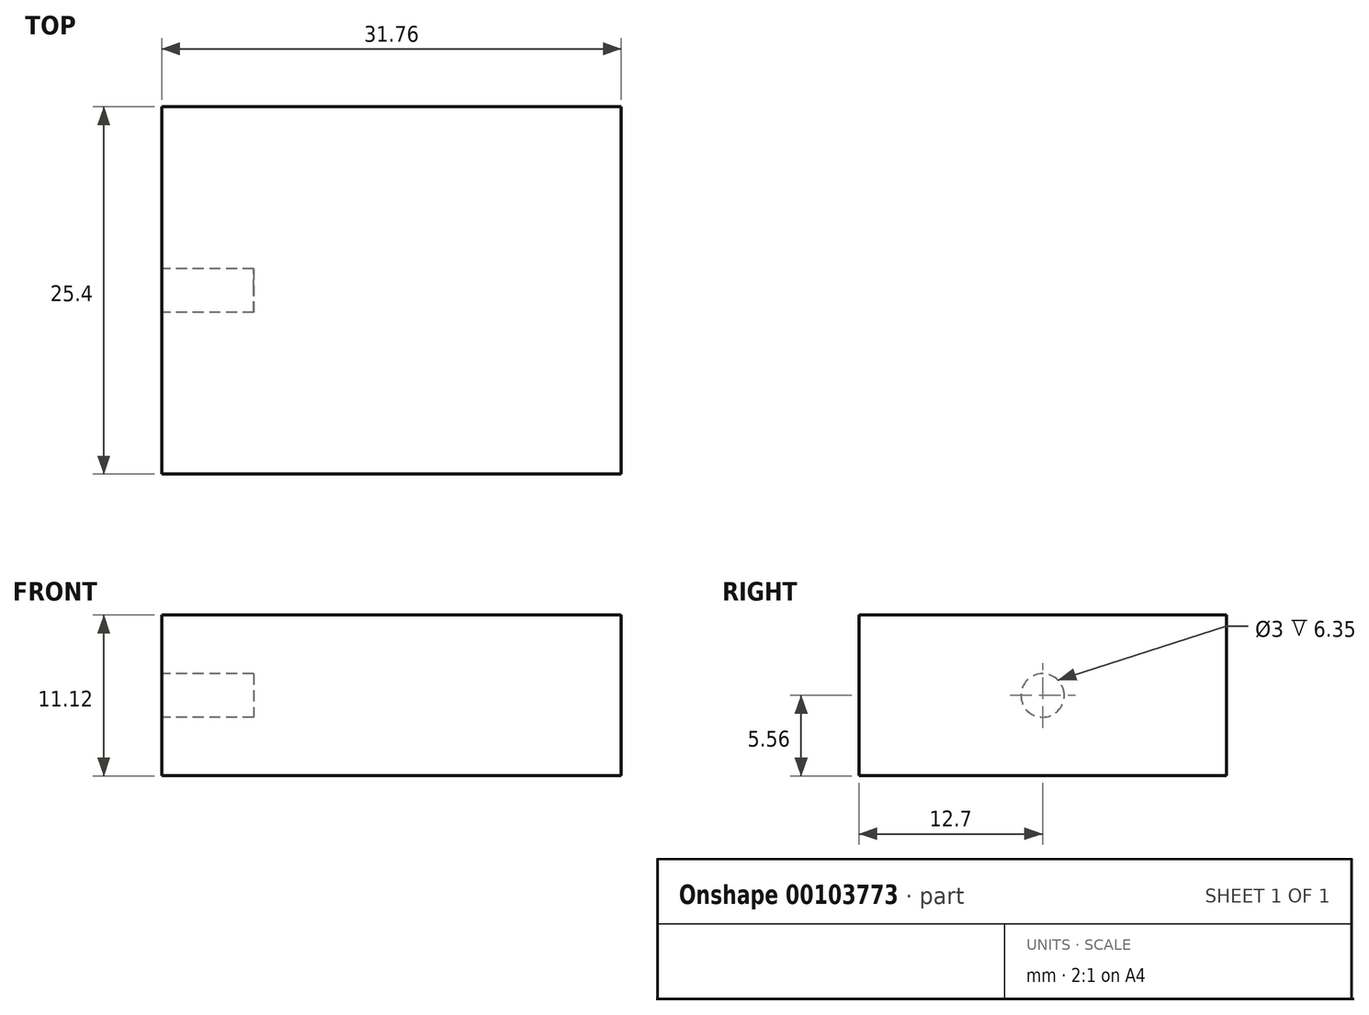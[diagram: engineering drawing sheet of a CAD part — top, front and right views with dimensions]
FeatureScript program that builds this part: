
annotation { "Feature Type Name" : "Feature", "Feature Type Description" : "" }
export const myFeature = defineFeature(function(context is Context, id is Id, definition is map)
    precondition{}
    {
        {
            var Q0;
            Q0=qCreatedBy(makeId("Front.planeOp"),FACE);
            var sketch = newSketch(context, id + "F0", { "sketchPlane" : qUnion([Q0])});
            skLineSegment(sketch, "E0.bottom", {"start": v(15.88, 5.56) * mm, "end": v(-15.88, 5.56) * mm});
            skLineSegment(sketch, "E0.top", {"start": v(15.88, -5.56) * mm, "end": v(-15.88, -5.56) * mm});
            skLineSegment(sketch, "E0.left", {"start": v(15.88, 5.56) * mm, "end": v(15.88, -5.56) * mm});
            skLineSegment(sketch, "E0.right", {"start": v(-15.88, 5.56) * mm, "end": v(-15.88, -5.56) * mm});
            skPoint(sketch, "E0.middle", {"position": v(0, 0) * mm});
            skSolve(sketch);
        }
        {
            var Q0;
            Q0=makeQuery(id+"F0.imprint","IMPRINT",FACE,{"disambiguationData":[TD([[makeQuery(id+"F0.imprint","IMPRINT",EDGE,{"derivedFrom":sQuery(id+"F0.wireOp",EDGE,"E0.bottom")}),1.0]])]});
            extrude(context, id + "F1", {"entities" : qUnion([Q0]), "depth" : 25.4 * mm});
        }
        {
            var Q0;
            Q0=makeQuery(id+"F1.opExtrude","SWEPT_FACE",FACE,{"disambiguationData":[OSD([sQuery(id+"F0.wireOp",EDGE,"E0.right")])]});
            var sketch = newSketch(context, id + "F2", { "sketchPlane" : qUnion([Q0])});
            skCircle(sketch, "E1", {"center": v(12.7, 0) * mm, "radius": 1.5 * mm});
            skPoint(sketch, "E2.start.orphan", {"position": v(25.4, 0) * mm});
            skPoint(sketch, "E3.trimOffspring.end.orphan", {"position": v(12.7, -5.56) * mm});
            skPoint(sketch, "E4.trimOffspring.end.orphan", {"position": v(0, 0) * mm});
            skPoint(sketch, "E5.start.orphan", {"position": v(12.7, 5.56) * mm});
            skLineSegment(sketch, "E6", {"start": v(12.7, -5.56) * mm, "end": v(12.7, 0) * mm});
            skSolve(sketch);
        }
        {
            var Q0;
            Q0=makeQuery(id+"F2.imprint","IMPRINT",FACE,{"disambiguationData":[TD([[makeQuery(id+"F2.imprint","IMPRINT",EDGE,{"derivedFrom":sQuery(id+"F2.wireOp",EDGE,"E1")}),1.0]])]});
            extrude(context, id + "F3", {"entities" : qUnion([Q0]), "operationType" : NewBodyOperationType.REMOVE, "oppositeDirection" : true, "depth" : 6.35 * mm});
        }
    });
